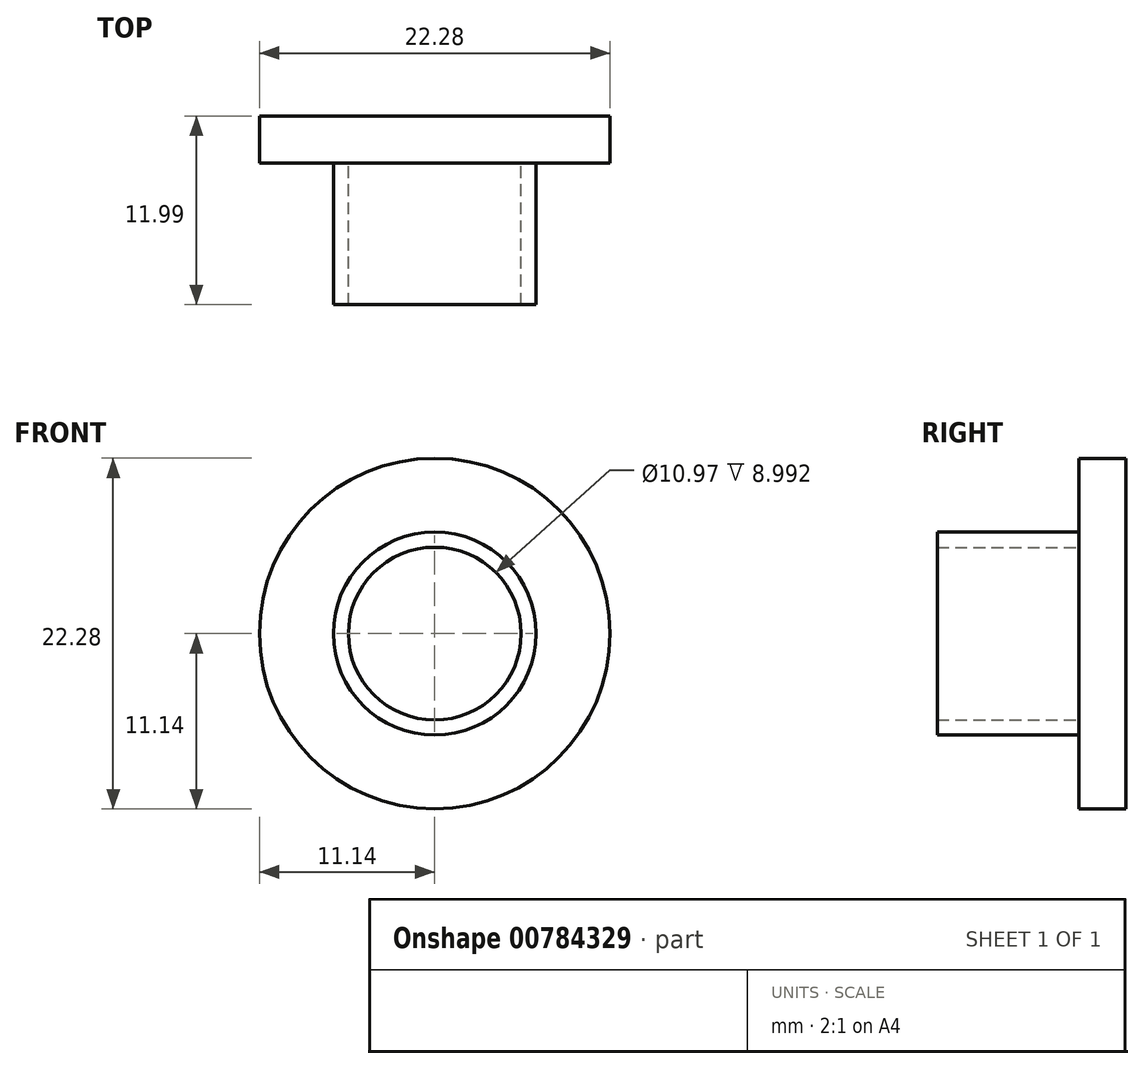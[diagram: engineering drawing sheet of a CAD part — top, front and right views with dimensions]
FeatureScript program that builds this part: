
annotation { "Feature Type Name" : "Feature", "Feature Type Description" : "" }
export const myFeature = defineFeature(function(context is Context, id is Id, definition is map)
    precondition{}
    {
        {
            var Q0;
            Q0=qCreatedBy(makeId("Front.planeOp"),FACE);
            var sketch = newSketch(context, id + "F0", { "sketchPlane" : qUnion([Q0])});
            skCircle(sketch, "E0", {"center": v(0, 0) * mm, "radius": 11.14 * mm});
            skSolve(sketch);
        }
        {
            var Q0;
            Q0=makeQuery(id+"F0.imprint","IMPRINT",FACE,{"disambiguationData":[TD([[makeQuery(id+"F0.imprint","IMPRINT",EDGE,{"derivedFrom":sQuery(id+"F0.wireOp",EDGE,"E0")}),1.0]])]});
            extrude(context, id + "F1", {"entities" : qUnion([Q0]), "depth" : 3 * mm, "offsetDistance" : 25.4 * mm});
        }
        {
            var Q0;
            Q0=qCreatedBy(makeId("Front.planeOp"),FACE);
            var sketch = newSketch(context, id + "F2", { "sketchPlane" : qUnion([Q0])});
            skCircle(sketch, "E1", {"center": v(0, 0) * mm, "radius": 6.44 * mm});
            skCircle(sketch, "E2", {"center": v(0, 0) * mm, "radius": 5.49 * mm});
            skSolve(sketch);
        }
        {
            var Q0;
            Q0 = qSketchRegion(id + "F2", true);
            extrude(context, id + "F3", {"entities" : qUnion([Q0]), "operationType" : NewBodyOperationType.ADD, "depth" : 12 * mm, "offsetDistance" : 25.4 * mm});
        }
    });
